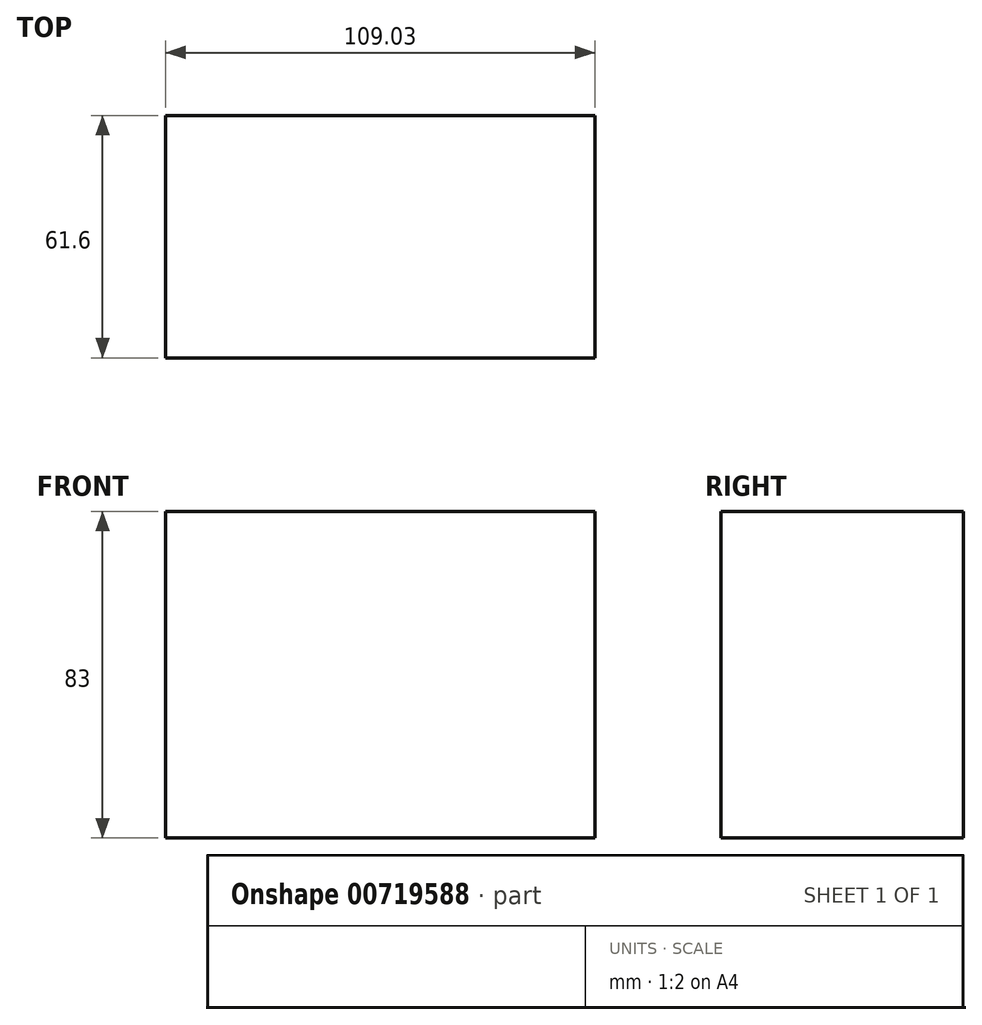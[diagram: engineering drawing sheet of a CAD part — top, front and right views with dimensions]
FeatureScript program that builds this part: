
annotation { "Feature Type Name" : "Feature", "Feature Type Description" : "" }
export const myFeature = defineFeature(function(context is Context, id is Id, definition is map)
    precondition{}
    {
        {
            var Q0;
            Q0=qCreatedBy(makeId("Top.planeOp"),FACE);
            var sketch = newSketch(context, id + "F0", { "sketchPlane" : qUnion([Q0])});
            skLineSegment(sketch, "E0.bottom", {"start": v(-30.07, -17.6) * mm, "end": v(78.96, -17.6) * mm});
            skLineSegment(sketch, "E0.top", {"start": v(-30.07, 44) * mm, "end": v(78.96, 44) * mm});
            skLineSegment(sketch, "E0.left", {"start": v(-30.07, -17.6) * mm, "end": v(-30.07, 44) * mm});
            skLineSegment(sketch, "E0.right", {"start": v(78.96, -17.6) * mm, "end": v(78.96, 44) * mm});
            skSolve(sketch);
        }
        {
            var Q0;
            Q0=sQuery(id+"F0.wireOp",EDGE,"E0.bottom");
            var Q1;
            Q1=sQuery(id+"F0.wireOp",EDGE,"E0.left");
            var Q2;
            Q2=sQuery(id+"F0.wireOp",EDGE,"E0.top");
            var Q3;
            Q3=sQuery(id+"F0.wireOp",EDGE,"E0.right");
            extrude(context, id + "F1", {"bodyType" : ToolBodyType.SURFACE, "surfaceEntities" : qUnion([Q0, Q1, Q2, Q3]), "depth" : 83 * mm, "offsetDistance" : 25 * mm});
        }
    });
